# Revit family: Displays_Cable_ASHanging_P-End
name_source: partatom
category: Generic Models
units: mm (PartAtom-declared; Revit-internal decimal feet)

## family parameters
Always vertical = No
Can host rebar = No
Classification Number = 23.40.90.11
Cut with Voids When Loaded = No
Maintain Annotation Orientation = No
Part Type = Normal
Room Calculation Point = No
Round Connector Dimension = Use Diameter
Shared = Yes
Work Plane-Based = Yes

## types (1)
- Stainless Steel
    Assembly Code = C1030500
    Cable = Stainless Steel
    Default Elevation = 4' - 0"
    Description = AS Hanging P End Cable
    EndLength = 0' - 1 11/64"
    Has Tensioner = Yes
    Hook = Stainless Steel
    Installation-Fabrication = https://www.ashanging.com
    Keynote = 10 14 00
    Manufacturer = AS Hanging
    Manufacturer Website = https://www.ashanging.com
    Model = P End Cable
    Product Data = http://www.arcat.com
    Product Properties = https://www.ashanging.com
    Revision = R1_2017
    Sales Information = https://www.ashanging.com
    Specification = http://www.arcat.com
    Tensioner Location = 0' - 1 3/4"
    URL = https://www.ashanging.com

## geometry (parser evidence)
native form markers: Sweep x5
no freeform markers — native parametric forms only
